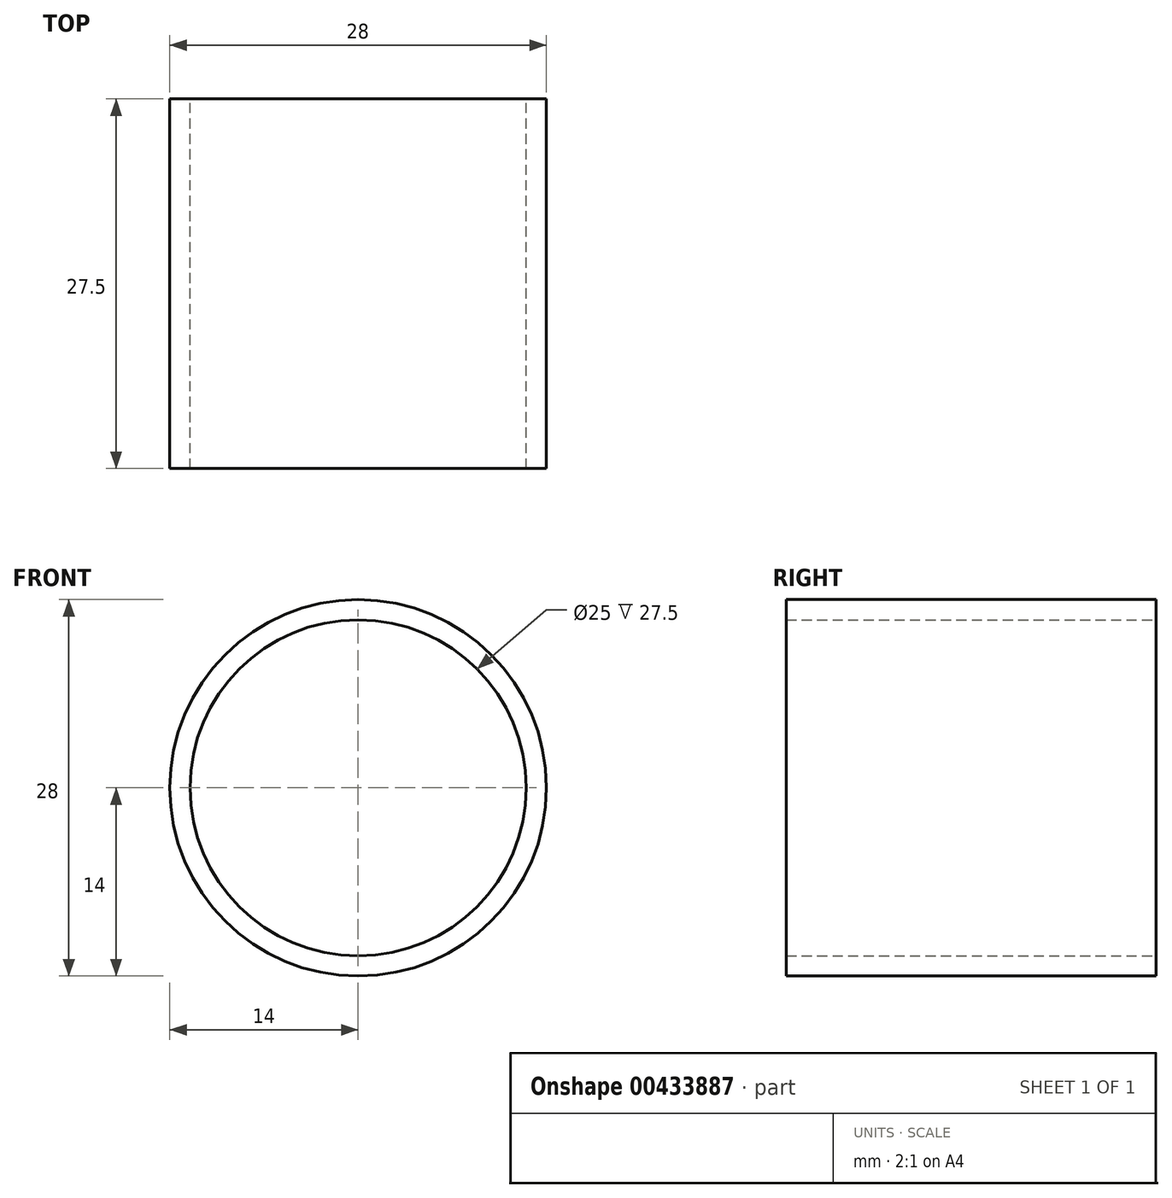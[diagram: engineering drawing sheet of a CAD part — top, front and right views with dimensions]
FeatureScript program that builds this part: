
annotation { "Feature Type Name" : "Feature", "Feature Type Description" : "" }
export const myFeature = defineFeature(function(context is Context, id is Id, definition is map)
    precondition{}
    {
        {
            var Q0;
            Q0=qCreatedBy(makeId("Front.planeOp"),FACE);
            var sketch = newSketch(context, id + "F0", { "sketchPlane" : qUnion([Q0])});
            skCircle(sketch, "E0", {"center": v(0, 0) * mm, "radius": 14 * mm});
            skCircle(sketch, "E1", {"center": v(0, 0) * mm, "radius": 12.5 * mm});
            skSolve(sketch);
        }
        {
            var Q0;
            Q0=makeQuery(id+"F0.imprint","IMPRINT",FACE,{"disambiguationData":[TD([[makeQuery(id+"F0.imprint","IMPRINT",EDGE,{"derivedFrom":sQuery(id+"F0.wireOp",EDGE,"E0")}),1.0]])]});
            extrude(context, id + "F1", {"entities" : qUnion([Q0]), "depth" : 27.5 * mm});
        }
    });
